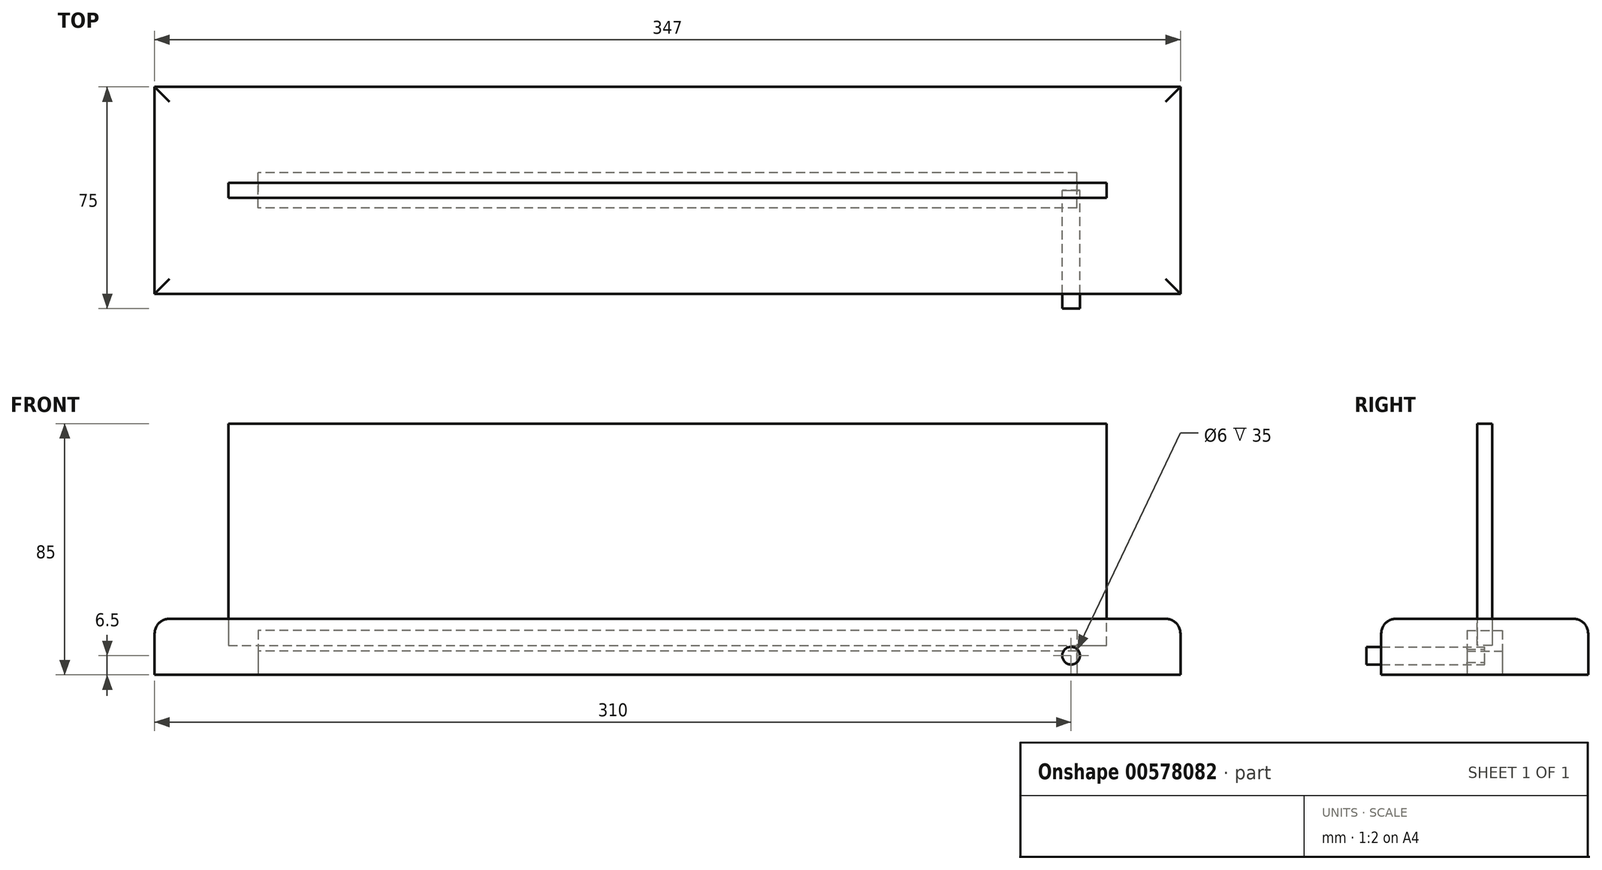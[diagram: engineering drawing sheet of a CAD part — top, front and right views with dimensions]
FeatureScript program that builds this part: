
annotation { "Feature Type Name" : "Feature", "Feature Type Description" : "" }
export const myFeature = defineFeature(function(context is Context, id is Id, definition is map)
    precondition{}
    {
        {
            assignVariable(context, id + "F0", {"name" : "SignThickness", "anyValue" : 5});
        }
        {
            var Q0;
            Q0=qCreatedBy(makeId("Front.planeOp"),FACE);
            var sketch = newSketch(context, id + "F1", { "sketchPlane" : qUnion([Q0])});
            skLineSegment(sketch, "E0", {"start": v(0, 0) * mm, "end": v(0, 16) * mm});
            skLineSegment(sketch, "E1", {"start": v(0, 16) * mm, "end": v(148.5, 16) * mm});
            skLineSegment(sketch, "E2", {"start": v(148.5, 16) * mm, "end": v(148.5, 91) * mm});
            skLineSegment(sketch, "E3", {"start": v(148.5, 91) * mm, "end": v(-148.5, 91) * mm});
            skLineSegment(sketch, "E4", {"start": v(-148.5, 91) * mm, "end": v(-148.5, 16) * mm});
            skLineSegment(sketch, "E5", {"start": v(-148.5, 16) * mm, "end": v(0, 16) * mm});
            skSolve(sketch);
        }
        {
            var Q0;
            Q0 = qSketchRegion(id + "F1", true);
            extrude(context, id + "F2", {"entities" : qUnion([Q0]), "endBound" : BoundingType.SYMMETRIC, "depth" : (getVariable(context, 'SignThickness')) * mm, "offsetDistance" : 25 * mm});
        }
        {
            var Q0;
            Q0=qCreatedBy(makeId("Top.planeOp"),FACE);
            var sketch = newSketch(context, id + "F3", { "sketchPlane" : qUnion([Q0])});
            skLineSegment(sketch, "E6.bottom", {"start": v(173.5, -35) * mm, "end": v(-173.5, -35) * mm});
            skLineSegment(sketch, "E6.top", {"start": v(173.5, 35) * mm, "end": v(-173.5, 35) * mm});
            skLineSegment(sketch, "E6.left", {"start": v(173.5, -35) * mm, "end": v(173.5, 35) * mm});
            skLineSegment(sketch, "E6.right", {"start": v(-173.5, -35) * mm, "end": v(-173.5, 35) * mm});
            skPoint(sketch, "E6.middle", {"position": v(0, 0) * mm});
            skSolve(sketch);
        }
        {
            var Q0;
            Q0 = qSketchRegion(id + "F3", true);
            extrude(context, id + "F4", {"entities" : qUnion([Q0]), "depth" : 19 * mm, "offsetDistance" : 25 * mm});
        }
        {
            var Q0;
            Q0=qCreatedBy(makeId("Top.planeOp"),FACE);
            var sketch = newSketch(context, id + "F5", { "sketchPlane" : qUnion([Q0])});
            skLineSegment(sketch, "E7.bottom", {"start": v(138.5, -6) * mm, "end": v(-138.5, -6) * mm});
            skLineSegment(sketch, "E7.top", {"start": v(138.5, 6) * mm, "end": v(-138.5, 6) * mm});
            skLineSegment(sketch, "E7.left", {"start": v(138.5, -6) * mm, "end": v(138.5, 6) * mm});
            skLineSegment(sketch, "E7.right", {"start": v(-138.5, -6) * mm, "end": v(-138.5, 6) * mm});
            skPoint(sketch, "E7.middle", {"position": v(0, 0) * mm});
            skSolve(sketch);
        }
        {
            var Q0;
            Q0 = qSketchRegion(id + "F5", true);
            extrude(context, id + "F6", {"entities" : qUnion([Q0]), "depth" : 15 * mm, "offsetDistance" : 25 * mm});
        }
        {
            var Q0;
            Q0=makeQuery(id+"F4.opExtrude","CAP_EDGE",EDGE,{"disambiguationData":[OSD([sQuery(id+"F3.wireOp",EDGE,"E6.bottom")])],"isStart":false});
            var Q1;
            Q1=makeQuery(id+"F4.opExtrude","CAP_EDGE",EDGE,{"disambiguationData":[OSD([sQuery(id+"F3.wireOp",EDGE,"E6.right")])],"isStart":false});
            var Q2;
            Q2=makeQuery(id+"F4.opExtrude","CAP_EDGE",EDGE,{"disambiguationData":[OSD([sQuery(id+"F3.wireOp",EDGE,"E6.left")])],"isStart":false});
            var Q3;
            Q3=makeQuery(id+"F4.opExtrude","CAP_EDGE",EDGE,{"disambiguationData":[OSD([sQuery(id+"F3.wireOp",EDGE,"E6.top")])],"isStart":false});
            fillet(context, id + "F7", {"entities" : qUnion([Q0, Q1, Q2, Q3]), "radius" : 5 * mm, "tangentPropagation" : true, "allowEdgeOverflow" : false});
        }
        {
            var Q0;
            Q0=makeQuery(id+"F2.opExtrude","SWEPT_BODY",BODY,{"disambiguationData":[OSD([sQuery(id+"F1.wireOp",EDGE,"E1"),sQuery(id+"F1.wireOp",EDGE,"E2"),sQuery(id+"F1.wireOp",EDGE,"E3"),sQuery(id+"F1.wireOp",EDGE,"E4"),sQuery(id+"F1.wireOp",EDGE,"E5")])]});
            transform(context, id + "F8", {"entities" : qUnion([Q0]), "transformType" : TransformType.TRANSLATION_3D, "dx" : 0 * mm, "dy" : 0 * mm, "dz" : -6 * mm, "makeCopy" : false});
        }
        {
            var Q0;
            Q0=makeQuery(id+"F2.opExtrude","SWEPT_BODY",BODY,{"disambiguationData":[OSD([sQuery(id+"F1.wireOp",EDGE,"E1"),sQuery(id+"F1.wireOp",EDGE,"E2"),sQuery(id+"F1.wireOp",EDGE,"E3"),sQuery(id+"F1.wireOp",EDGE,"E4"),sQuery(id+"F1.wireOp",EDGE,"E5")])]});
            var Q1;
            Q1=makeQuery(id+"F6.opExtrude","SWEPT_BODY",BODY,{"disambiguationData":[OSD([sQuery(id+"F5.wireOp",EDGE,"E7.bottom"),sQuery(id+"F5.wireOp",EDGE,"E7.top"),sQuery(id+"F5.wireOp",EDGE,"E7.left"),sQuery(id+"F5.wireOp",EDGE,"E7.right")])]});
            var Q2;
            Q2=makeQuery(id+"F4.opExtrude","SWEPT_BODY",BODY,{"disambiguationData":[OSD([sQuery(id+"F3.wireOp",EDGE,"E6.bottom"),sQuery(id+"F3.wireOp",EDGE,"E6.top"),sQuery(id+"F3.wireOp",EDGE,"E6.left"),sQuery(id+"F3.wireOp",EDGE,"E6.right")])]});
            booleanBodies(context, id + "F9", {"operationType" : BooleanOperationType.SUBTRACTION, "tools" : qUnion([Q0, Q1]), "targets" : qUnion([Q2]), "keepTools" : true});
        }
        {
            var Q0;
            Q0=qCreatedBy(makeId("Front.planeOp"),FACE);
            var sketch = newSketch(context, id + "F10", { "sketchPlane" : qUnion([Q0])});
            skLineSegment(sketch, "E8", {"start": v(0, 0) * mm, "end": v(0, 6.5) * mm});
            skLineSegment(sketch, "E9", {"start": v(0, 6.5) * mm, "end": v(136.5, 6.5) * mm});
            skCircle(sketch, "E10", {"center": v(136.5, 6.5) * mm, "radius": 3 * mm});
            skSolve(sketch);
        }
        {
            var Q0;
            Q0 = qSketchRegion(id + "F10", true);
            extrude(context, id + "F11", {"entities" : qUnion([Q0]), "depth" : 40 * mm, "offsetDistance" : 25 * mm});
        }
        {
            var Q0;
            Q0=makeQuery(id+"F11.opExtrude","SWEPT_BODY",BODY,{"disambiguationData":[OSD([sQuery(id+"F10.wireOp",EDGE,"E10")])]});
            var Q1;
            Q1=makeQuery(id+"F4.opExtrude","SWEPT_BODY",BODY,{"disambiguationData":[OSD([sQuery(id+"F3.wireOp",EDGE,"E6.bottom"),sQuery(id+"F3.wireOp",EDGE,"E6.top"),sQuery(id+"F3.wireOp",EDGE,"E6.left"),sQuery(id+"F3.wireOp",EDGE,"E6.right")])]});
            booleanBodies(context, id + "F12", {"operationType" : BooleanOperationType.SUBTRACTION, "tools" : qUnion([Q0]), "targets" : qUnion([Q1]), "keepTools" : true});
        }
        {
            var Q0;
            Q0=qCreatedBy(makeId("Top.planeOp"),FACE);
            var sketch = newSketch(context, id + "F13", { "sketchPlane" : qUnion([Q0])});
            skLineSegment(sketch, "E11.bottom", {"start": v(138.5, -6) * mm, "end": v(-138.5, -6) * mm});
            skLineSegment(sketch, "E11.top", {"start": v(138.5, 6) * mm, "end": v(-138.5, 6) * mm});
            skLineSegment(sketch, "E11.left", {"start": v(138.5, -6) * mm, "end": v(138.5, 6) * mm});
            skLineSegment(sketch, "E11.right", {"start": v(-138.5, -6) * mm, "end": v(-138.5, 6) * mm});
            skPoint(sketch, "E11.middle", {"position": v(0, 0) * mm});
            skSolve(sketch);
        }
        {
            var Q0;
            Q0 = qSketchRegion(id + "F13", true);
            extrude(context, id + "F14", {"entities" : qUnion([Q0]), "depth" : 8 * mm, "offsetDistance" : 25 * mm});
        }
    });
